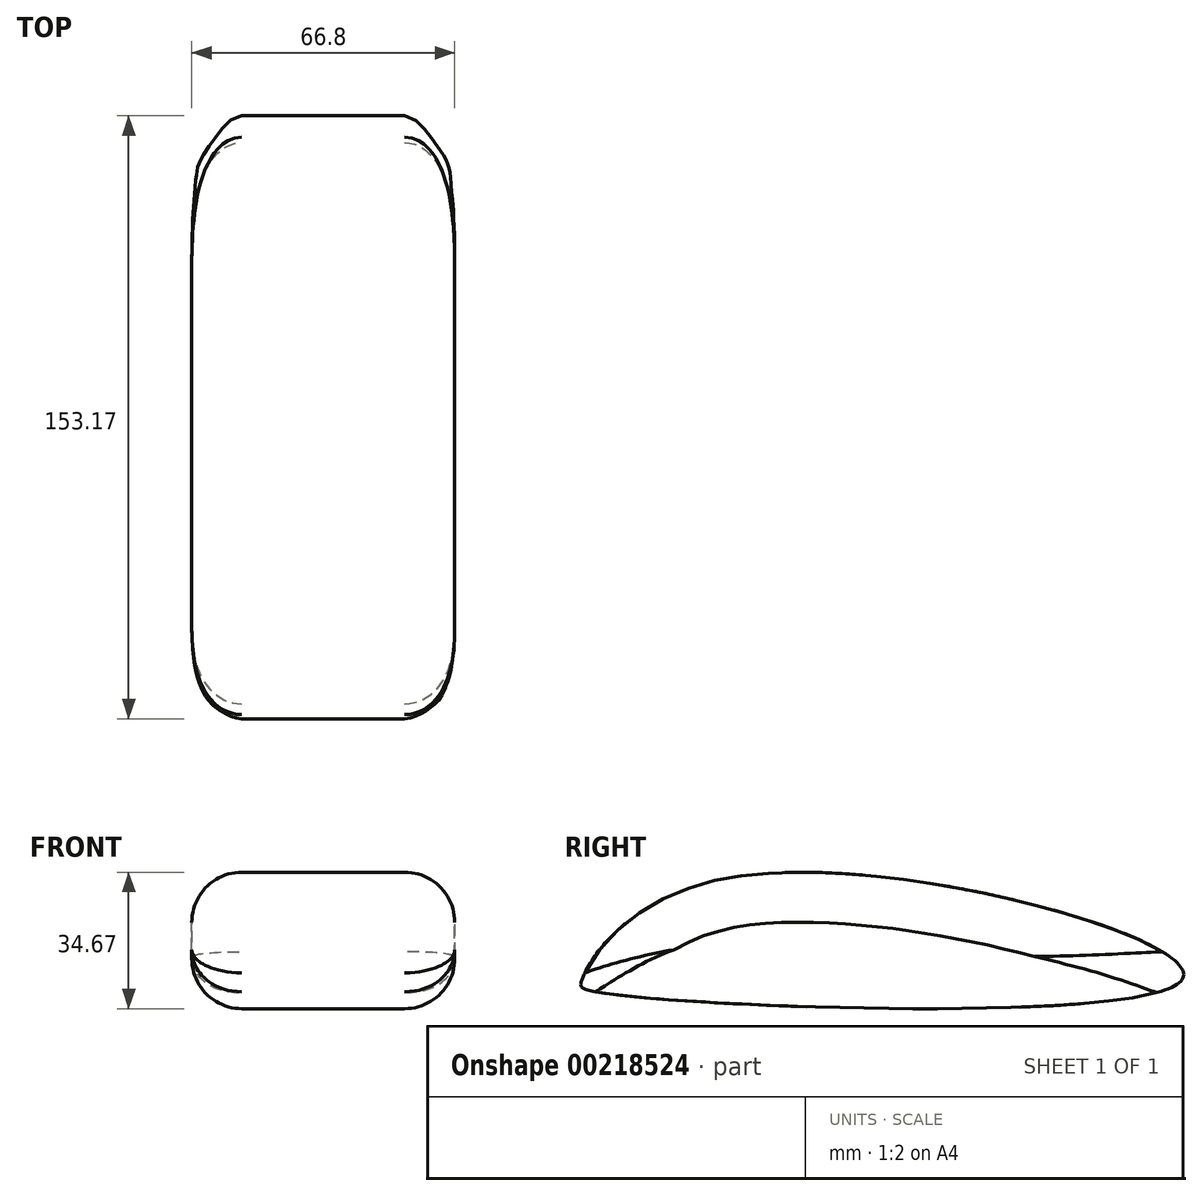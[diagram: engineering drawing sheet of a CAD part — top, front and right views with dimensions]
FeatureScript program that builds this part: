
annotation { "Feature Type Name" : "Feature", "Feature Type Description" : "" }
export const myFeature = defineFeature(function(context is Context, id is Id, definition is map)
    precondition{}
    {
        {
            var Q0;
            Q0=qCreatedBy(makeId("Right.planeOp"),FACE);
            var sketch = newSketch(context, id + "F0", { "sketchPlane" : qUnion([Q0])});
            skFitSpline(sketch, "E0", {"points": [v(-76.19, 0) * mm, v(-39.05, 26.1) * mm, v(76.19, 0) * mm, v(-74.07, -2.55) * mm, v(-76.19, 0) * mm]});
            skSolve(sketch);
        }
        {
            var Q0;
            Q0 = qSketchRegion(id + "F0", true);
            extrude(context, id + "F1", {"entities" : qUnion([Q0]), "depth" : 66.8 * mm});
        }
        {
            var Q0;
            Q0=makeQuery(id+"F1.opExtrude","CAP_EDGE",EDGE,{"disambiguationData":[OSD([sQuery(id+"F0.wireOp",EDGE,"E0")])],"isStart":false});
            fillet(context, id + "F2", {"entities" : qUnion([Q0]), "radius" : 12.7 * mm, "tangentPropagation" : true, "allowEdgeOverflow" : false});
        }
        {
            var Q0;
            Q0=makeQuery(id+"F1.opExtrude","CAP_EDGE",EDGE,{"disambiguationData":[OSD([sQuery(id+"F0.wireOp",EDGE,"E0")])],"isStart":true});
            fillet(context, id + "F3", {"entities" : qUnion([Q0]), "radius" : 12.7 * mm, "tangentPropagation" : true, "allowEdgeOverflow" : false});
        }
    });
